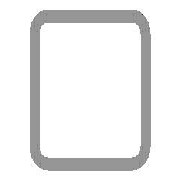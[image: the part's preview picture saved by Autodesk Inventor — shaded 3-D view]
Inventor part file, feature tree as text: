
AUTODESK INVENTOR PART (.ipt)
format: ipt  version: 2025.3 (Build 293356030, 356C)  size: 154,112 bytes
history: native  units: mm (DEFAULTED — no unit token found)
features: other x4, plane x3, split x2, sketch x1
ambient origin geometry x8: Origin, YZ Plane, XZ Plane, XY Plane, X Axis, Y Axis, Z Axis, Center Point
bodies: Solid1 (feature_tree), Body (feature_tree)
feature tree (10):
  parser-record x1  (decoder bookkeeping rows leaked as tree rows — omitted from the tree; the rows remain in map.json)
  other  "Driven Length"
  other  "Start Plane"
  other  "End Plane"
  plane  "Work Plane4"
  split  "Split1"
  plane  "Work Plane5"
  split  "Split2"
  sketch  "Sketch3"  dims[d3=2216.344931mm d4=0.0mm d7=6.0mm d9=80.0mm d11=80.0mm d12=3.0mm d13=-14.545455mm d14=2201.799476mm d15=40.0mm d16=40.0mm d17=90.0deg d18=2216.344931mm]
  plane  "Work Plane3"
